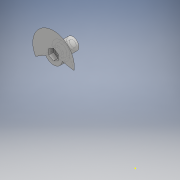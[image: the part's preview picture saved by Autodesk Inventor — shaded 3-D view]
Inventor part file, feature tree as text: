
AUTODESK INVENTOR PART (.ipt)
format: ipt  version: 2017 (Build 210142000, 142)  size: 147,968 bytes
history: native  units: mm
features: sketch x6, extrude x4, plane x1, revolve x1, projected_geometry x1
ambient origin geometry x8: Origin, YZ Plane, XZ Plane, XY Plane, X Axis, Y Axis, Z Axis, Center Point
bodies: Solid1 (feature_tree)
feature tree (13):
  extrude  "Extrusion1"  Depth=6.25mm TaperAngle=0.0deg
  extrude  "Extrusion2"  Depth=2.25mm TaperAngle=0.0deg
  extrude  "Extrusion3"  Depth=10.0mm TaperAngle=0.0deg
  sketch  "Sketch4"  dims[d12=38.397244mm]
  extrude  "Extrusion4"  [1 undecoded]
  plane  "Work Plane1"
  revolve  "Revolution1"  [1 undecoded]
  sketch  "Sketch1"  dims[d2=8.0mm d3=6.25mm d4=0.0mm]
  sketch  "Sketch2"  dims[d5=5.5mm d6=2.25mm d7=0.0mm]
  sketch  "Sketch3"  dims[d8=5.75mm d9=0.0mm d10=10.0mm d11=0.0mm]
  projected_geometry  "Projected Loop1"
  sketch  "Sketch5"
  sketch  "Sketch8"
note: 2 required parameter values undecoded (feature->parameter linkage not recoverable at this tier; creation-order binding heuristic only, values carry confidence <= 0.55)
